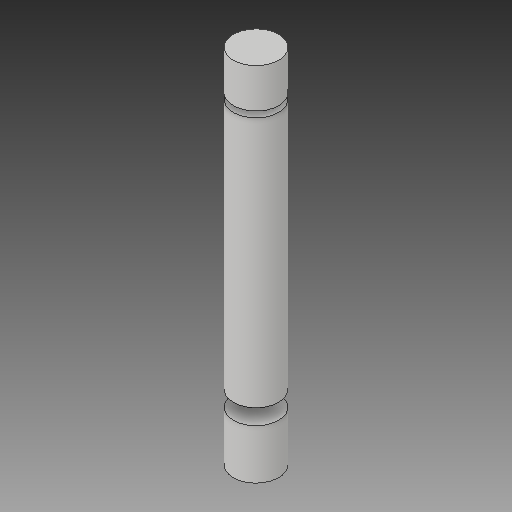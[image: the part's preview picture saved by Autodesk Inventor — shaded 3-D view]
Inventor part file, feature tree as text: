
AUTODESK INVENTOR PART (.ipt)
format: ipt  version: 2017 (Build 210142000, 142)  size: 122,880 bytes
history: native  units: in
note: dims shown in document units (in); Inventor stores cm internally (conversion verified against a paired STEP export)
features: extrude x2, sketch x2, projected_geometry x1
ambient origin geometry x8: Origin, YZ Plane, XZ Plane, XY Plane, X Axis, Y Axis, Z Axis, Center Point
bodies: Body1 (feature_tree)
feature tree (5):
  extrude  "Extrusion2"  Depth=2.25in
  extrude  "Extrusion3"  Depth=1.955in
  sketch  "Sketch2"  dims[d3=18.0in d4=2.25in]
  sketch  "Sketch3"  dims[d5=0.295in d6=1.955in d7=0.775in d8=2.475in d9=2.25in d10=0.0in d11=2.25in d12=1.125in d13=1.125in d14=18.0in d15=0.0in]
  projected_geometry  "Projected Loop1"
